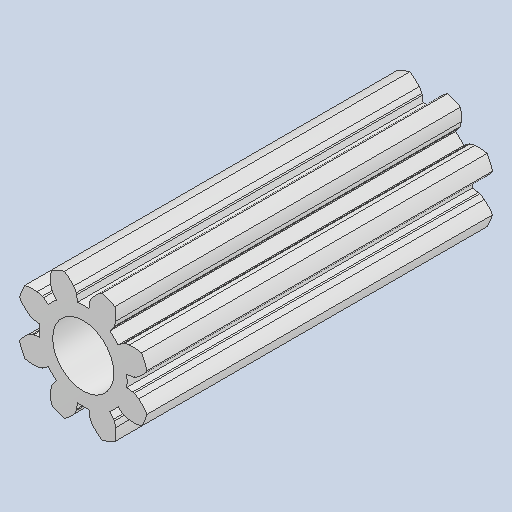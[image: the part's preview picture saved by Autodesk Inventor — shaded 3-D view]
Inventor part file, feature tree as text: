
AUTODESK INVENTOR PART (.ipt)
format: ipt  version: 2023 (Build 270158030, 158C)  size: 249,856 bytes
history: native  units: mm
features: extrude x1, sketch x1
ambient origin geometry x8: Origin, YZ Plane, XZ Plane, XY Plane, X Axis, Y Axis, Z Axis, Center Point
bodies: Body1 (feature_tree)
feature tree (2):
  extrude  "Extrusion2"  Depth=13.0mm
  sketch  "Sketch2"  dims[d3=13.0mm d4=0.0mm d6=2.3mm]
